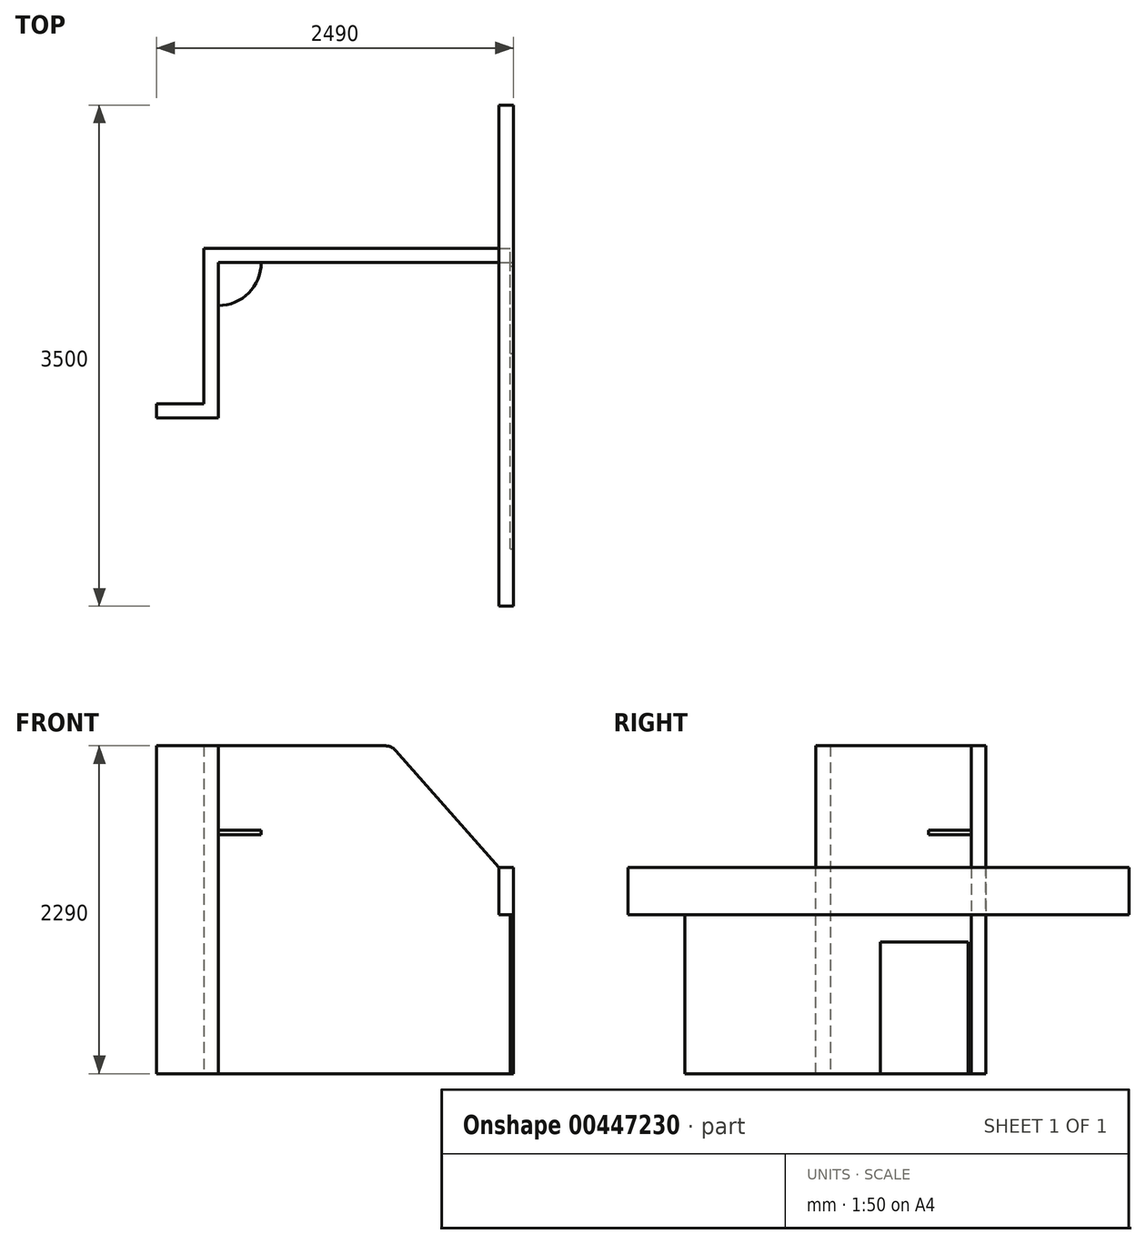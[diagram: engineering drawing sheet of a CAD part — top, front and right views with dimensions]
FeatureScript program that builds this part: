
annotation { "Feature Type Name" : "Feature", "Feature Type Description" : "" }
export const myFeature = defineFeature(function(context is Context, id is Id, definition is map)
    precondition{}
    {
        {
            var Q0;
            Q0=qCreatedBy(makeId("Front.planeOp"),FACE);
            var sketch = newSketch(context, id + "F0", { "sketchPlane" : qUnion([Q0])});
            skLineSegment(sketch, "E0", {"start": v(0, 2290) * mm, "end": v(0, 0) * mm});
            skLineSegment(sketch, "E1", {"start": v(0, 2290) * mm, "end": v(1164.87, 2290) * mm});
            skLineSegment(sketch, "E2", {"start": v(1960, 1440) * mm, "end": v(1960, 1110) * mm});
            skLineSegment(sketch, "E3", {"start": v(1960, 1110) * mm, "end": v(2040, 1110) * mm});
            skLineSegment(sketch, "E4", {"start": v(2040, 1110) * mm, "end": v(2040, 0) * mm});
            skLineSegment(sketch, "E5", {"start": v(0, 0) * mm, "end": v(2040, 0) * mm});
            skLineSegment(sketch, "E6", {"start": v(1239.86, 2256.16) * mm, "end": v(1960, 1440) * mm});
            skPoint(sketch, "E7.visualSharp", {"position": v(1210, 2290) * mm});
            skArc(sketch, "E7.filletArc", {"start": v(1239.86, 2256.16) * mm, "mid": v(1206, 2281.15) * mm, "end": v(1164.87, 2290) * mm});
            skSolve(sketch);
        }
        {
            var Q0;
            Q0=makeQuery(id+"F0.imprint","IMPRINT",FACE,{"disambiguationData":[TD([[makeQuery(id+"F0.imprint","IMPRINT",EDGE,{"derivedFrom":sQuery(id+"F0.wireOp",EDGE,"E0")}),1.0]])]});
            extrude(context, id + "F1", {"entities" : qUnion([Q0]), "depth" : 100 * mm});
        }
        {
            var Q0;
            Q0=qCreatedBy(makeId("Right.planeOp"),FACE);
            var sketch = newSketch(context, id + "F2", { "sketchPlane" : qUnion([Q0])});
            skLineSegment(sketch, "E8.bottom", {"start": v(0, 0) * mm, "end": v(-1186, 0) * mm});
            skLineSegment(sketch, "E8.top", {"start": v(0, 2290) * mm, "end": v(-1186, 2290) * mm});
            skLineSegment(sketch, "E8.left", {"start": v(0, 0) * mm, "end": v(0, 2290) * mm});
            skLineSegment(sketch, "E8.right", {"start": v(-1186, 0) * mm, "end": v(-1186, 2290) * mm});
            skSolve(sketch);
        }
        {
            var Q0;
            Q0=makeQuery(id+"F2.imprint","IMPRINT",FACE,{"disambiguationData":[TD([[makeQuery(id+"F2.imprint","IMPRINT",EDGE,{"derivedFrom":sQuery(id+"F2.wireOp",EDGE,"E8.bottom")}),-1.0]])]});
            extrude(context, id + "F3", {"entities" : qUnion([Q0]), "operationType" : NewBodyOperationType.ADD, "oppositeDirection" : true, "depth" : 100 * mm});
        }
        {
            var Q0;
            Q0=qCreatedBy(makeId("Front.planeOp"),FACE);
            var sketch = newSketch(context, id + "F4", { "sketchPlane" : qUnion([Q0])});
            skLineSegment(sketch, "E9", {"start": v(1960, 1440) * mm, "end": v(2060, 1440) * mm});
            skLineSegment(sketch, "E10", {"start": v(2060, 1440) * mm, "end": v(2060, 1110) * mm});
            skLineSegment(sketch, "E11", {"start": v(2060, 1110) * mm, "end": v(1960, 1110) * mm});
            skLineSegment(sketch, "E12", {"start": v(1960, 1110) * mm, "end": v(1960, 1440) * mm});
            skSolve(sketch);
        }
        {
            var Q0;
            Q0=makeQuery(id+"F4.imprint","IMPRINT",FACE,{"disambiguationData":[TD([[makeQuery(id+"F4.imprint","IMPRINT",EDGE,{"derivedFrom":sQuery(id+"F4.wireOp",EDGE,"E9")}),-1.0]])]});
            extrude(context, id + "F5", {"entities" : qUnion([Q0]), "depth" : 2500 * mm, "hasSecondDirection" : true, "secondDirectionOppositeDirection" : true, "secondDirectionDepth" : 1000 * mm});
        }
        {
            var Q0;
            Q0=makeQuery(id+"F3.opExtrude","CAP_FACE",FACE,{"disambiguationData":[OSD([sQuery(id+"F2.wireOp",EDGE,"E8.bottom"),sQuery(id+"F2.wireOp",EDGE,"E8.top"),sQuery(id+"F2.wireOp",EDGE,"E8.left"),sQuery(id+"F2.wireOp",EDGE,"E8.right")])],"isStart":false});
            var sketch = newSketch(context, id + "F6", { "sketchPlane" : qUnion([Q0])});
            skLineSegment(sketch, "E13.bottom", {"start": v(1186, 2290) * mm, "end": v(1086, 2290) * mm});
            skLineSegment(sketch, "E13.top", {"start": v(1186, 0) * mm, "end": v(1086, 0) * mm});
            skLineSegment(sketch, "E13.left", {"start": v(1186, 2290) * mm, "end": v(1186, 0) * mm});
            skLineSegment(sketch, "E13.right", {"start": v(1086, 2290) * mm, "end": v(1086, 0) * mm});
            skSolve(sketch);
        }
        {
            var Q0;
            Q0=makeQuery(id+"F6.imprint","IMPRINT",FACE,{"disambiguationData":[TD([[makeQuery(id+"F6.imprint","IMPRINT",EDGE,{"derivedFrom":sQuery(id+"F6.wireOp",EDGE,"E13.bottom")}),-1.0]])]});
            extrude(context, id + "F7", {"entities" : qUnion([Q0]), "operationType" : NewBodyOperationType.ADD, "depth" : 330 * mm});
        }
        {
            var Q0;
            Q0=makeQuery(id+"F1.opExtrude","CAP_FACE",FACE,{"disambiguationData":[OSD([sQuery(id+"F0.wireOp",EDGE,"E0"),sQuery(id+"F0.wireOp",EDGE,"E1"),sQuery(id+"F0.wireOp",EDGE,"E2"),sQuery(id+"F0.wireOp",EDGE,"E3"),sQuery(id+"F0.wireOp",EDGE,"E4"),sQuery(id+"F0.wireOp",EDGE,"E5"),sQuery(id+"F0.wireOp",EDGE,"E6")])],"isStart":false});
            var sketch = newSketch(context, id + "F8", { "sketchPlane" : qUnion([Q0])});
            skLineSegment(sketch, "E14.bottom", {"start": v(2040, 1110) * mm, "end": v(2060, 1110) * mm});
            skLineSegment(sketch, "E14.top", {"start": v(2040, 0) * mm, "end": v(2060, 0) * mm});
            skLineSegment(sketch, "E14.left", {"start": v(2040, 1110) * mm, "end": v(2040, 0) * mm});
            skLineSegment(sketch, "E14.right", {"start": v(2060, 1110) * mm, "end": v(2060, 0) * mm});
            skSolve(sketch);
        }
        {
            var Q0;
            Q0 = qSketchRegion(id + "F8", true);
            var Q1;
            Q1 = qConstructionFilter(qBodyType(qCreatedBy(id + "F8" ,EDGE), BodyType.WIRE), ConstructionObject.NO);
            extrude(context, id + "F9", {"entities" : qUnion([Q0]), "surfaceEntities" : qUnion([Q1]), "depth" : 2000 * mm});
        }
        {
            var Q0;
            Q0=makeQuery(id+"F9.opExtrude","SWEPT_FACE",FACE,{"disambiguationData":[OSD([sQuery(id+"F8.wireOp",EDGE,"E14.right")])]});
            var sketch = newSketch(context, id + "F10", { "sketchPlane" : qUnion([Q0])});
            skLineSegment(sketch, "E15.bottom", {"start": v(-735, 0) * mm, "end": v(-125, 0) * mm});
            skLineSegment(sketch, "E15.top", {"start": v(-735, 920) * mm, "end": v(-125, 920) * mm});
            skLineSegment(sketch, "E15.left", {"start": v(-735, 0) * mm, "end": v(-735, 920) * mm});
            skLineSegment(sketch, "E15.right", {"start": v(-125, 0) * mm, "end": v(-125, 920) * mm});
            skSolve(sketch);
        }
        {
            var Q0;
            Q0=makeQuery(id+"F10.imprint","IMPRINT",FACE,{"disambiguationData":[TD([[makeQuery(id+"F10.imprint","IMPRINT",EDGE,{"derivedFrom":sQuery(id+"F10.wireOp",EDGE,"E15.bottom")}),1.0]])]});
            extrude(context, id + "F11", {"entities" : qUnion([Q0]), "operationType" : NewBodyOperationType.REMOVE, "oppositeDirection" : true, "depth" : 20 * mm});
        }
        {
            var Q0;
            Q0=qCreatedBy(makeId("Top.planeOp"),FACE);
            var sketch = newSketch(context, id + "F12", { "sketchPlane" : qUnion([Q0])});
            skLineSegment(sketch, "E16", {"start": v(0, -100) * mm, "end": v(0, -400) * mm});
            skLineSegment(sketch, "E17", {"start": v(300, -100) * mm, "end": v(0, -100) * mm});
            skArc(sketch, "E18", {"start": v(0, -400) * mm, "mid": v(212.13, -312.13) * mm, "end": v(300, -100) * mm});
            skSolve(sketch);
        }
        {
            var Q0;
            Q0=makeQuery(id+"F12.imprint","IMPRINT",FACE,{"disambiguationData":[TD([[makeQuery(id+"F12.imprint","IMPRINT",EDGE,{"derivedFrom":sQuery(id+"F12.wireOp",EDGE,"E16")}),1.0]])]});
            extrude(context, id + "F13", {"entities" : qUnion([Q0]), "operationType" : NewBodyOperationType.ADD, "depth" : 1700 * mm, "hasSecondDirection" : true, "secondDirectionOppositeDirection" : false, "secondDirectionDepth" : 1670 * mm});
        }
    });
